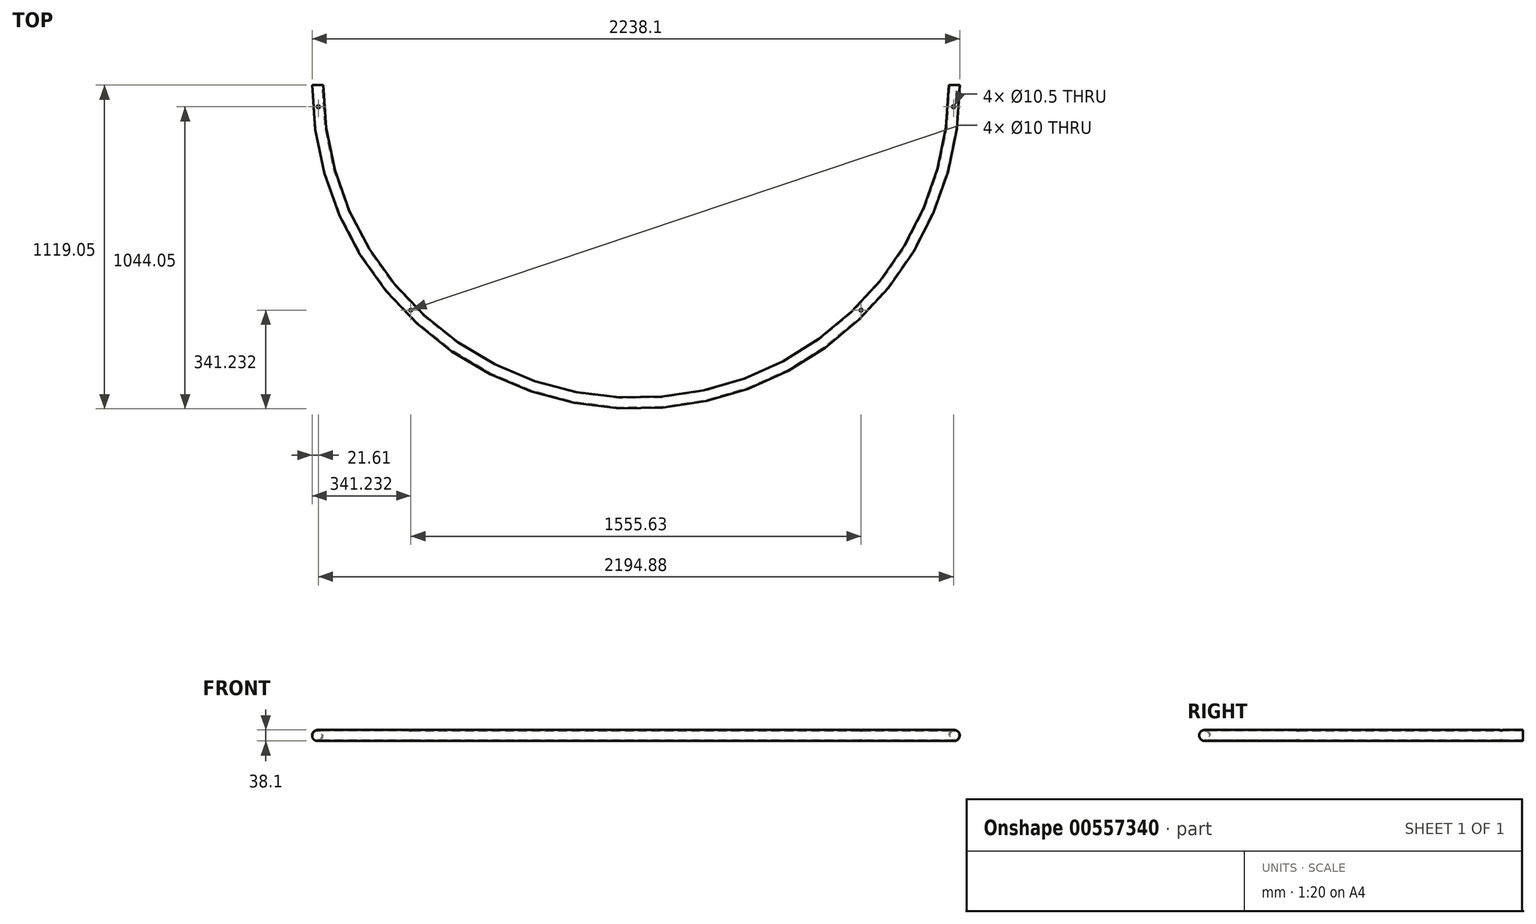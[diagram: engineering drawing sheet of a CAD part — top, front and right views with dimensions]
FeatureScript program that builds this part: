
annotation { "Feature Type Name" : "Feature", "Feature Type Description" : "" }
export const myFeature = defineFeature(function(context is Context, id is Id, definition is map)
    precondition{}
    {
        {
            var Q0;
            Q0=qCreatedBy(makeId("Front.planeOp"),FACE);
            var sketch = newSketch(context, id + "F0", { "sketchPlane" : qUnion([Q0])});
            skCircle(sketch, "E0", {"center": v(-1100, 0) * mm, "radius": 19.05 * mm});
            skCircle(sketch, "E1", {"center": v(-1100, 0) * mm, "radius": 15.85 * mm});
            skLineSegment(sketch, "E2", {"start": v(0, 0) * mm, "end": v(0, 380.17) * mm, "construction": true});
            skSolve(sketch);
        }
        {
            var Q0;
            Q0=qSketchRegion(id+"F0",true);
            var Q1;
            Q1=sQuery(id+"F0.wireOp",EDGE,"E2");
            revolve(context, id + "F1", {"entities" : qUnion([Q0]), "axis" : qUnion([Q1]), "revolveType" : RevolveType.ONE_DIRECTION, "angle" : 180 * degree});
        }
        {
            var Q0;
            Q0=qCreatedBy(makeId("Top.planeOp"),FACE);
            var sketch = newSketch(context, id + "F2", { "sketchPlane" : qUnion([Q0])});
            skArc(sketch, "E3", {"start": v(-1100, 0) * mm, "mid": v(0, -1100) * mm, "end": v(1100, 0) * mm, "construction": true});
            skCircle(sketch, "E4", {"center": v(-1097.44, -75) * mm, "radius": 5.25 * mm});
            skLineSegment(sketch, "E5", {"start": v(0, 0) * mm, "end": v(0, -1100) * mm, "construction": true});
            skCircle(sketch, "E6.MirrorC", {"center": v(1097.44, -75) * mm, "radius": 5.25 * mm});
            skSolve(sketch);
        }
        {
            var Q0;
            Q0=qSketchRegion(id+"F2",true);
            extrude(context, id + "F3", {"entities" : qUnion([Q0]), "operationType" : NewBodyOperationType.REMOVE, "endBound" : BoundingType.THROUGH_ALL, "oppositeDirection" : true, "depth" : 25 * mm, "offsetDistance" : 25 * mm, "hasSecondDirection" : true, "secondDirectionBound" : BoundingType.THROUGH_ALL, "secondDirectionOppositeDirection" : false, "secondDirectionDepth" : 25 * mm});
        }
        {
            var Q0;
            Q0=qCreatedBy(makeId("Top.planeOp"),FACE);
            var sketch = newSketch(context, id + "F4", { "sketchPlane" : qUnion([Q0])});
            skCircle(sketch, "E7", {"center": v(-777.82, -777.82) * mm, "radius": 5 * mm});
            skLineSegment(sketch, "E8", {"start": v(-777.82, -777.82) * mm, "end": v(0, 0) * mm, "construction": true});
            skCircle(sketch, "E9.MirrorC", {"center": v(777.82, -777.82) * mm, "radius": 5 * mm});
            skSolve(sketch);
        }
        {
            var Q0;
            Q0 = qSketchRegion(id + "F4", true);
            extrude(context, id + "F5", {"entities" : qUnion([Q0]), "operationType" : NewBodyOperationType.REMOVE, "endBound" : BoundingType.THROUGH_ALL, "oppositeDirection" : true, "depth" : 25 * mm, "offsetDistance" : 25 * mm, "hasSecondDirection" : true, "secondDirectionOppositeDirection" : false, "secondDirectionDepth" : 25 * mm});
        }
    });
